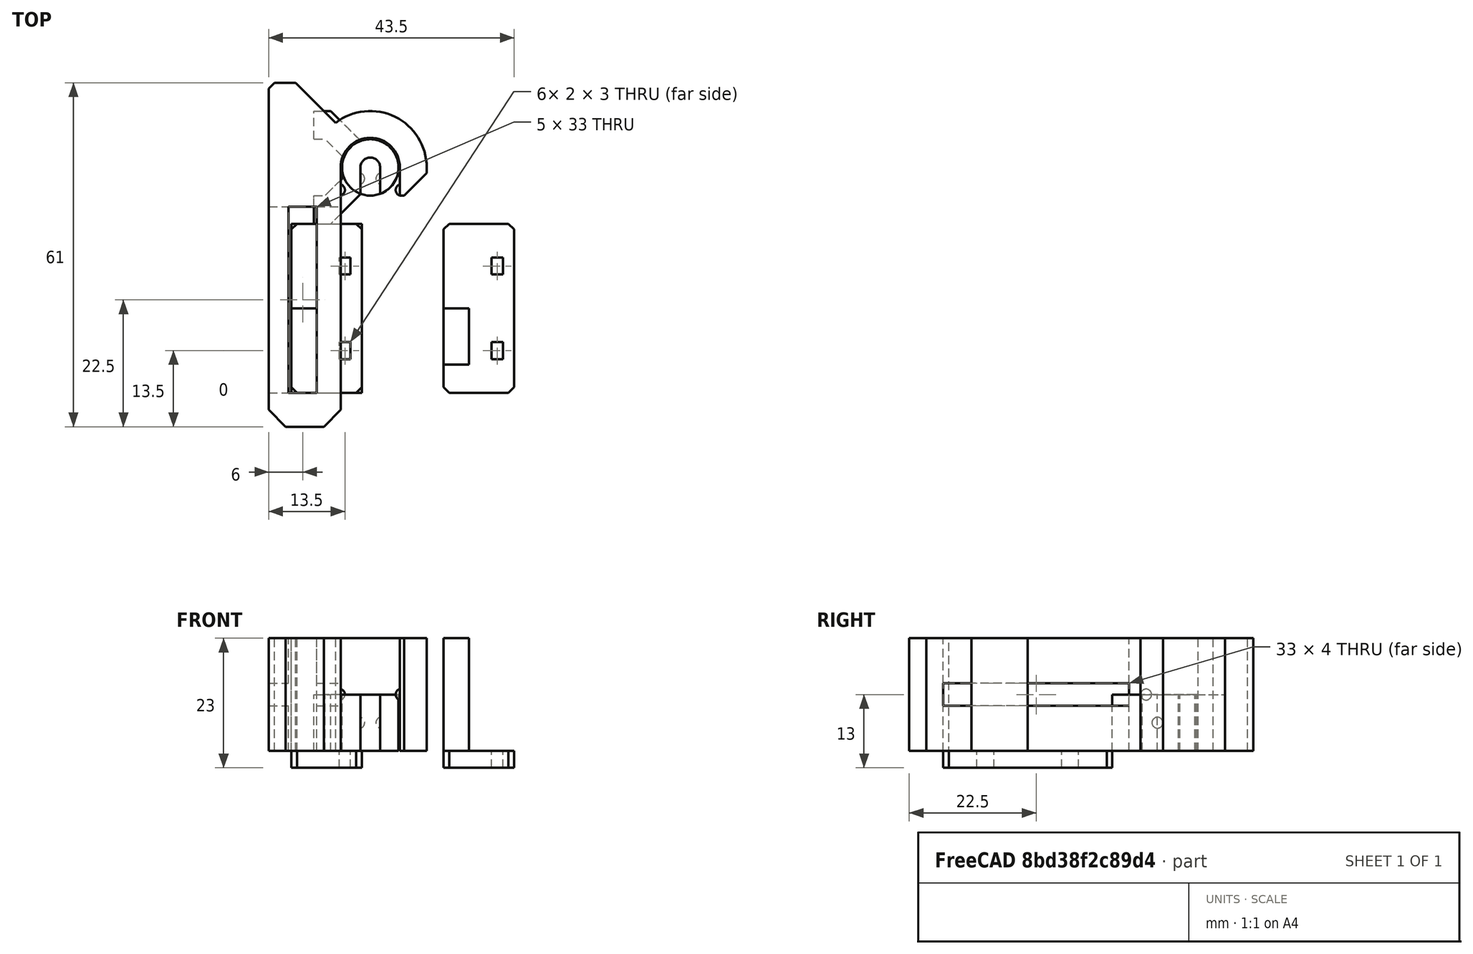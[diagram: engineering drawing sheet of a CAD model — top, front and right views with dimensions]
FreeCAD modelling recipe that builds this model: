
FCSTD DOCUMENT  (FreeCAD 0.18R16146 (Git))
Label: washing-rack-hanger
License: All rights reserved
LicenseURL: http://en.wikipedia.org/wiki/All_rights_reserved
objects: Part::Box×13, Part::Cut×9, Part::Chamfer×8, Part::Cylinder×5, Part::MultiFuse×5, Part::Sphere×4, Part::Feature×3
note: 47 computed .brp shape members not serialized (recipe doc carries the construction recipe); baked Part::Feature solids carry a one-line shape summary decoded from their .brp

FEATURE [Part::Cylinder] Cylinder
  Angle = 360
  AttacherType = Attacher::AttachEngine3D
  Height = 20
  Radius = 5.25
FEATURE [Part::Cylinder] Cylinder001
  Angle = 360
  AttacherType = Attacher::AttachEngine3D
  Height = 20
  Radius = 10
FEATURE [Part::Box] Box  label="Cube"
  AttacherType = Attacher::AttachEngine3D
  Height = 20
  Length = 12.75
  Placement = pos=(-18,-46,0) rot=(0,0,1;0rad)
  Width = 61
FEATURE [Part::Cut] Cut
  Base = -> Cylinder001
  Tool = -> Cylinder
FEATURE [Part::Chamfer] Chamfer
  Base = -> Box
  Edges = 1 edges r=8: [Edge7]
FEATURE [Part::Box] Box001  label="Cube001"
  AttacherType = Attacher::AttachEngine3D
  Height = 4
  Length = 19
  Placement = pos=(-21,-40,8) rot=(0,0,1;0rad)
  Width = 33
FEATURE [Part::Cut] Cut001
  Base = -> Chamfer
  Tool = -> Box001
FEATURE [Part::Box] Box002  label="Cube002"
  AttacherType = Attacher::AttachEngine3D
  Height = 20
  Length = 23
  Placement = pos=(-11,-11,0) rot=(0,0,1;0rad)
  Width = 11
FEATURE [Part::Cut] Cut002
  Base = -> Cut
  Tool = -> Box002
FEATURE [Part::Box] Box003  label="Cube003"
  AttacherType = Attacher::AttachEngine3D
  Height = 20
  Length = 4.75
  Placement = pos=(5.25,-5,0) rot=(0,0,1;0rad)
  Width = 5
FEATURE [Part::Cylinder] Cylinder002  label="pref"
  Angle = 360
  AttacherType = Attacher::AttachEngine3D
  Height = 10
  Radius = 5
FEATURE [Part::Sphere] Sphere
  Angle1 = -90
  Angle2 = 90
  Angle3 = 360
  AttacherType = Attacher::AttachEngine3D
  Placement = pos=(-5.5,-4,10) rot=(0,0,1;0rad)
  Radius = 1
FEATURE [Part::Sphere] Sphere001
  Angle1 = -90
  Angle2 = 90
  Angle3 = 360
  AttacherType = Attacher::AttachEngine3D
  Placement = pos=(5.5,-4,10) rot=(0,0,1;0rad)
  Radius = 1
FEATURE [Part::Chamfer] Chamfer001
  Base = -> Cut001
  Edges = 2 edges r=3: [Edge3,Edge16]
FEATURE [Part::Chamfer] Chamfer002
  Base = -> Chamfer001
  Edges = 1 edges r=1: [Edge32]
FEATURE [Part::Chamfer] Chamfer003
  Base = -> Box003
  Edges = 1 edges r=4: [Edge5]
FEATURE [Part::Box] Box004  label="Cube004"
  AttacherType = Attacher::AttachEngine3D
  Height = 20
  Length = 5
  Placement = pos=(-14.5,-40,0) rot=(0,0,1;0rad)
  Width = 33
FEATURE [Part::Box] Box005  label="Cube005"
  AttacherType = Attacher::AttachEngine3D
  Height = 20
  Length = 4.5
  Placement = pos=(-14,-40,0) rot=(0,0,1;0rad)
  Width = 15
FEATURE [Part::Cut] Cut003
  Base = -> Chamfer002
  Tool = -> Box004
FEATURE [Part::Box] Box006  label="Cube006"
  AttacherType = Attacher::AttachEngine3D
  Height = 3
  Length = 12.5
  Placement = pos=(-14,-40,-3) rot=(0,0,1;0rad)
  Width = 30
FEATURE [Part::Box] Box007  label="Cube007"
  AttacherType = Attacher::AttachEngine3D
  Height = 3
  Length = 2
  Placement = pos=(-5.5,-34,-3) rot=(0,0,1;0rad)
  Width = 3
FEATURE [Part::Box] Box008  label="Cube008"
  AttacherType = Attacher::AttachEngine3D
  Height = 3
  Length = 2
  Placement = pos=(-5.5,-19,-3) rot=(0,0,1;0rad)
  Width = 3
FEATURE [Part::MultiFuse] Fusion
  Shapes = -> [Box008,Box007]
FEATURE [Part::Cut] Cut004
  Base = -> Box006
  Tool = -> Fusion
FEATURE [Part::MultiFuse] Fusion001  label="lock"
  Shapes = -> [Box005,Cut004]
FEATURE [Part::MultiFuse] Fusion002
  Shapes = -> [Cut003,Cut002]
FEATURE [Part::MultiFuse] Fusion003  label="base"
  Shapes = -> [Fusion002,Chamfer003,Sphere,Sphere001]
FEATURE [Part::Feature] Fusion003001  label="base-exp"
  shape: bbox 28 x 61 x 20 mm, 43 faces (baked)
FEATURE [Part::Feature] Fusion001001  label="lock001"
  shape: bbox 12.5 x 30 x 23 mm, 17 faces (baked)
FEATURE [Part::Chamfer] Chamfer004  label="lock-btm-exp"
  Base = -> Fusion001001
  Edges = 4 edges r=1: [Edge23,Edge24,Edge36,Edge45]
FEATURE [Part::Feature] Fusion001002  label="lock002"
  Placement = pos=(27,0,0) rot=(0,0,1;0rad)
  shape: bbox 12.5 x 30 x 23 mm, 19 faces (baked)
FEATURE [Part::Box] Box009  label="Cube009"
  AttacherType = Attacher::AttachEngine3D
  Height = 21
  Length = 10
  Placement = pos=(11,-45,0) rot=(0,0,1;0rad)
  Width = 10
FEATURE [Part::Cut] Cut005
  Base = -> Fusion001002
  Tool = -> Box009
FEATURE [Part::Chamfer] Chamfer005  label="lock-top-exp"
  Base = -> Cut005
  Edges = 4 edges r=1: [Edge12,Edge15,Edge34,Edge37]
FEATURE [Part::Cylinder] Cylinder003  label="Cylinder002"
  Angle = 360
  AttacherType = Attacher::AttachEngine3D
  Height = 10
  Radius = 5
FEATURE [Part::Cylinder] Cylinder004  label="Cylinder003"
  Angle = 360
  AttacherType = Attacher::AttachEngine3D
  Height = 10
  Radius = 1.75
FEATURE [Part::Box] Box010  label="Cube010"
  AttacherType = Attacher::AttachEngine3D
  Height = 10
  Length = 8.25
  Placement = pos=(-10,-10,0) rot=(0,0,1;0rad)
  Width = 20
FEATURE [Part::Box] Box011  label="Cube011"
  AttacherType = Attacher::AttachEngine3D
  Height = 10
  Length = 3.5
  Placement = pos=(-1.75,-10,0) rot=(0,0,1;0rad)
  Width = 10
FEATURE [Part::Cut] Cut006
  Base = -> Cylinder003
  Tool = -> Cylinder004
FEATURE [Part::Cut] Cut007
  Base = -> Cut006
  Tool = -> Box011
FEATURE [Part::Chamfer] Chamfer006
  Base = -> Box010
  Edges = 2 edges r=5.25: [Edge5,Edge7]
FEATURE [Part::Sphere] Sphere002
  Angle1 = -90
  Angle2 = 90
  Angle3 = 360
  AttacherType = Attacher::AttachEngine3D
  Placement = pos=(-2,-2,5) rot=(0,0,1;0rad)
  Radius = 1
FEATURE [Part::Sphere] Sphere003
  Angle1 = -90
  Angle2 = 90
  Angle3 = 360
  AttacherType = Attacher::AttachEngine3D
  Placement = pos=(2,-2,5) rot=(0,0,1;0rad)
  Radius = 1
FEATURE [Part::Box] Box012  label="Cube012"
  AttacherType = Attacher::AttachEngine3D
  Height = 10
  Length = 5
  Placement = pos=(-10,-5,0) rot=(0,0,1;0rad)
  Width = 10
FEATURE [Part::Chamfer] Chamfer007
  Base = -> Box012
  Edges = 2 edges r=3: [Edge5,Edge7]
FEATURE [Part::Cut] Cut008
  Base = -> Chamfer006
  Tool = -> Chamfer007
FEATURE [Part::MultiFuse] Fusion003002  label="spacer"
  Shapes = -> [Cut008,Sphere003,Sphere002,Cut007]
